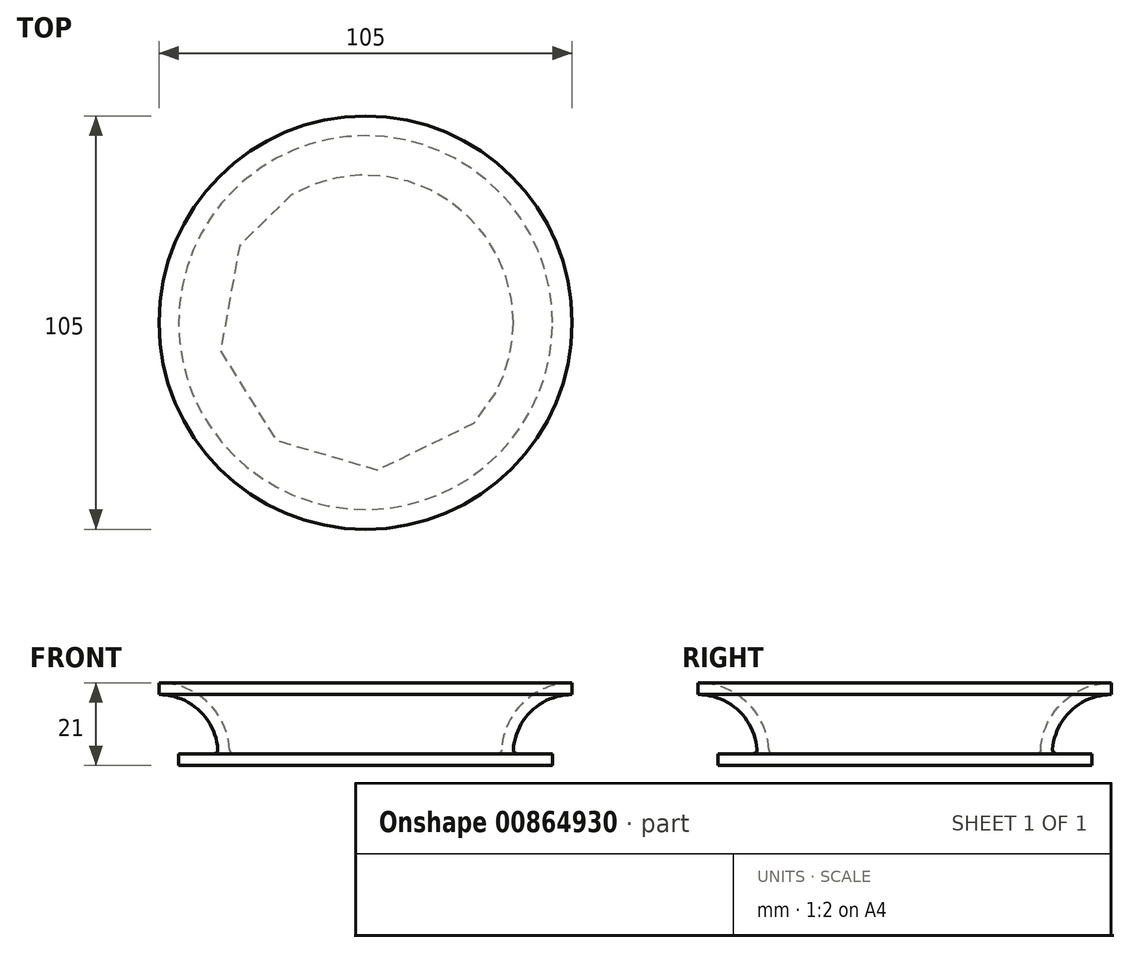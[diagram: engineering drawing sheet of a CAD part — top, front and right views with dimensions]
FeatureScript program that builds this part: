
annotation { "Feature Type Name" : "Feature", "Feature Type Description" : "" }
export const myFeature = defineFeature(function(context is Context, id is Id, definition is map)
    precondition{}
    {
        {
            var Q0;
            Q0=qCreatedBy(makeId("Front.planeOp"),FACE);
            var sketch = newSketch(context, id + "F0", { "sketchPlane" : qUnion([Q0])});
            skLineSegment(sketch, "E0.bottom", {"start": v(0, 0) * mm, "end": v(47.5, 0) * mm});
            skLineSegment(sketch, "E0.top", {"start": v(0, 3) * mm, "end": v(47.5, 3) * mm});
            skLineSegment(sketch, "E0.left", {"start": v(0, 0) * mm, "end": v(0, 3) * mm});
            skLineSegment(sketch, "E0.right", {"start": v(47.5, 0) * mm, "end": v(47.5, 3) * mm});
            skLineSegment(sketch, "E1", {"start": v(37.5, 0) * mm, "end": v(37.5, 40) * mm, "construction": true});
            skArc(sketch, "E2", {"start": v(37.5, 3) * mm, "mid": v(41.9, 13.6) * mm, "end": v(52.5, 18) * mm});
            skArc(sketch, "E3", {"start": v(34.5, 3) * mm, "mid": v(39.77, 15.73) * mm, "end": v(52.5, 21) * mm});
            skLineSegment(sketch, "E4", {"start": v(52.5, 21) * mm, "end": v(52.5, 18) * mm});
            skLineSegment(sketch, "E5", {"start": v(0, 45.23) * mm, "end": v(0, -54.77) * mm, "construction": true});
            skLineSegment(sketch, "E6", {"start": v(47.5, 32.6) * mm, "end": v(47.5, -17.4) * mm, "construction": true});
            skSolve(sketch);
        }
        {
            var Q0;
            Q0 = qSketchRegion(id + "F0", true);
            var Q1;
            Q1=sQuery(id+"F0.wireOp",EDGE,"E5");
            revolve(context, id + "F1", {"surfaceOperationType" : NewSurfaceOperationType.NEW, "entities" : qUnion([Q0]), "axis" : qUnion([Q1]), "revolveType" : RevolveType.FULL});
        }
        {
            var Q0;
            Q0=makeQuery(id+"F1.opRevolve","SWEPT_EDGE",EDGE,{"disambiguationData":[OSD([sQuery(id+"F0.wireOp",EDGE,"E0.top"),sQuery(id+"F0.wireOp",EDGE,"E3")])]});
            var Q1;
            Q1=makeQuery(id+"F1.opRevolve","SWEPT_EDGE",EDGE,{"disambiguationData":[OSD([sQuery(id+"F0.wireOp",EDGE,"E0.top"),sQuery(id+"F0.wireOp",EDGE,"E2")])]});
            fillet(context, id + "F2", {"entities" : qUnion([Q0, Q1]), "radius" : 1 * mm, "tangentPropagation" : true, "allowEdgeOverflow" : false});
        }
    });
